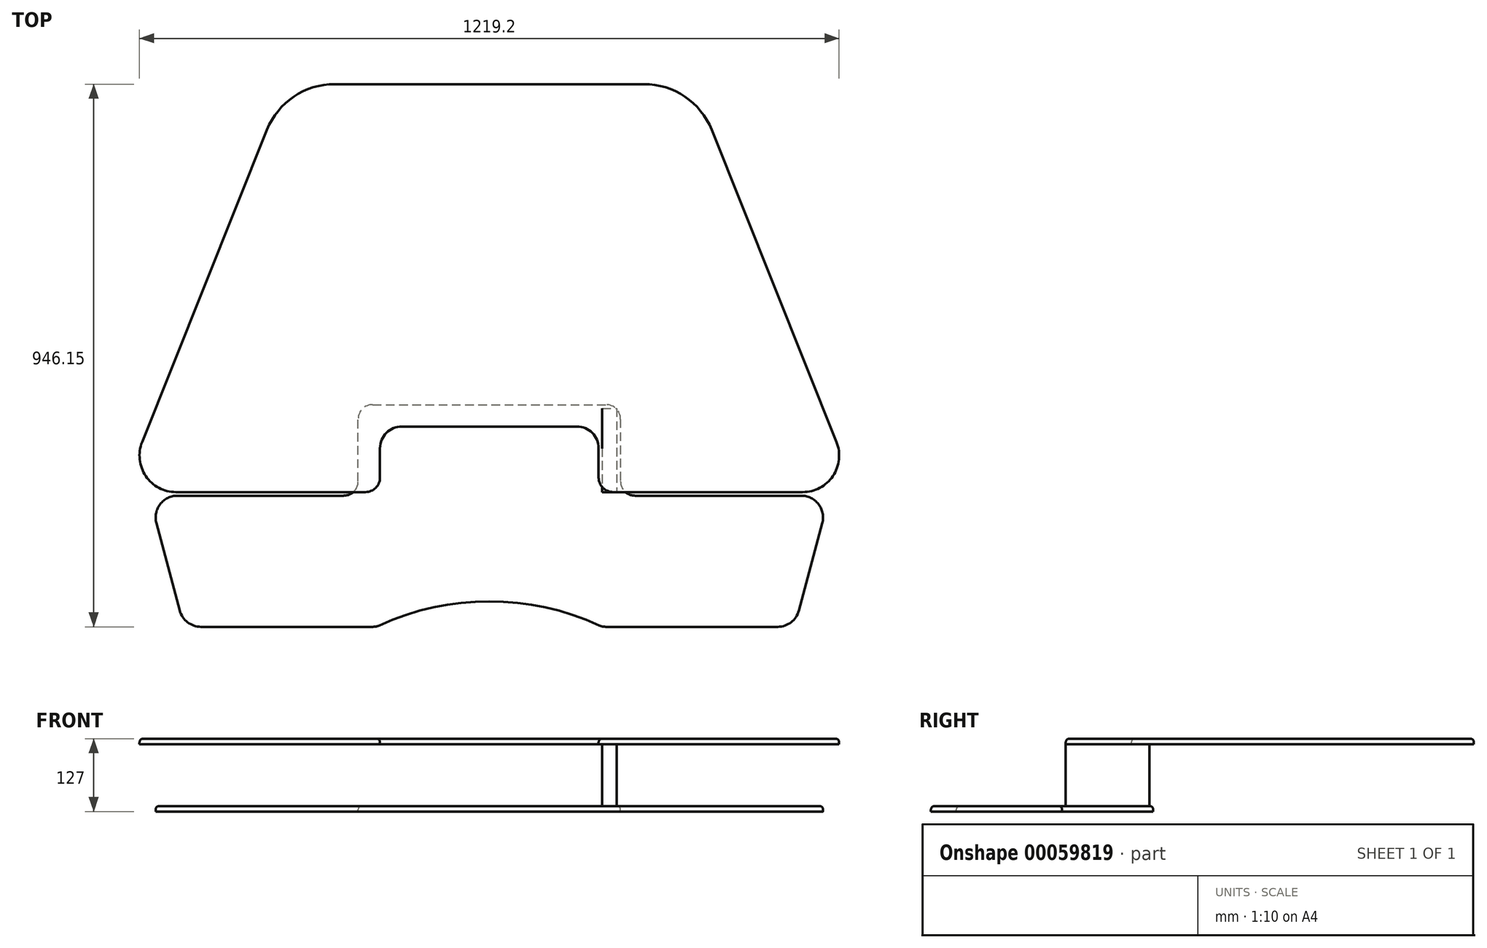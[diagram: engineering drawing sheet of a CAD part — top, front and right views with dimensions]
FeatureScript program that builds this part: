
annotation { "Feature Type Name" : "Feature", "Feature Type Description" : "" }
export const myFeature = defineFeature(function(context is Context, id is Id, definition is map)
    precondition{}
    {
        {
            var Q0;
            Q0=qCreatedBy(makeId("Top.planeOp"),FACE);
            var sketch = newSketch(context, id + "F0", { "sketchPlane" : qUnion([Q0])});
            skLineSegment(sketch, "E0", {"start": v(-190.5, 114.3) * mm, "end": v(190.5, 114.3) * mm});
            skLineSegment(sketch, "E1", {"start": v(190.5, 114.3) * mm, "end": v(190.5, 0) * mm});
            skLineSegment(sketch, "E2", {"start": v(190.5, 0) * mm, "end": v(546.1, 0) * mm});
            skLineSegment(sketch, "E3", {"start": v(605.06, 87.07) * mm, "end": v(355.6, 711.2) * mm});
            skLineSegment(sketch, "E4", {"start": v(355.6, 711.2) * mm, "end": v(-355.6, 711.2) * mm});
            skArc(sketch, "E5.filletArc", {"start": v(546.1, 0) * mm, "mid": v(598.68, 27.9) * mm, "end": v(605.06, 87.07) * mm});
            skLineSegment(sketch, "E6", {"start": v(0, 711.2) * mm, "end": v(0, 114.3) * mm, "construction": true});
            skLineSegment(sketch, "E7.MirrorCS", {"start": v(-605.06, 87.07) * mm, "end": v(-355.6, 711.2) * mm});
            skArc(sketch, "E8.MirrorCS", {"start": v(-546.1, 0) * mm, "mid": v(-598.68, 27.9) * mm, "end": v(-605.06, 87.07) * mm});
            skLineSegment(sketch, "E9.MirrorCS", {"start": v(-190.5, 0) * mm, "end": v(-546.1, 0) * mm});
            skLineSegment(sketch, "E10.MirrorCS", {"start": v(-190.5, 114.3) * mm, "end": v(-190.5, 0) * mm});
            skPoint(sketch, "E11.MirrorCS.end.orphan", {"position": v(0, 711.2) * mm});
            skPoint(sketch, "E11.MirrorCS.start.orphan", {"position": v(-355.6, 711.2) * mm});
            skPoint(sketch, "E12.MirrorCS.end.orphan", {"position": v(-190.5, 114.3) * mm});
            skPoint(sketch, "E12.MirrorCS.start.orphan", {"position": v(0, 114.3) * mm});
            skSolve(sketch);
        }
        {
            var Q0;
            Q0=qCreatedBy(makeId("Top.planeOp"),FACE);
            cPlane(context, id + "F1", {"entities" : qUnion([Q0]), "cplaneType" : CPlaneType.OFFSET, "offset" : 107.95 * mm, "oppositeDirection" : true, "width" : 152.4 * mm, "height" : 152.4 * mm});
        }
        {
            var Q0;
            Q0=qCreatedBy(id+"F1.planeOp",FACE);
            var sketch = newSketch(context, id + "F2", { "sketchPlane" : qUnion([Q0])});
            skLineSegment(sketch, "E13.bottom", {"start": v(-543.47, -6.35) * mm, "end": v(-254, -6.35) * mm});
            skLineSegment(sketch, "E13.top", {"start": v(-502.64, -234.95) * mm, "end": v(-202.3, -234.95) * mm});
            skLineSegment(sketch, "E13.left", {"start": v(-580.27, -54.31) * mm, "end": v(-539.44, -206.71) * mm});
            skLineSegment(sketch, "E13.right", {"start": v(580.27, -54.31) * mm, "end": v(539.44, -206.71) * mm});
            skLineSegment(sketch, "E14", {"start": v(-228.6, 19.05) * mm, "end": v(-228.6, 127) * mm});
            skLineSegment(sketch, "E15", {"start": v(-203.2, 152.4) * mm, "end": v(203.2, 152.4) * mm});
            skLineSegment(sketch, "E16", {"start": v(228.6, 127) * mm, "end": v(228.6, 19.05) * mm});
            skLineSegment(sketch, "E17.trimOffspring", {"start": v(254, -6.35) * mm, "end": v(543.47, -6.35) * mm});
            skPoint(sketch, "E18.visualSharp", {"position": v(-228.6, 152.4) * mm});
            skArc(sketch, "E18.filletArc", {"start": v(-203.2, 152.4) * mm, "mid": v(-221.16, 144.96) * mm, "end": v(-228.6, 127) * mm});
            skPoint(sketch, "E19.visualSharp", {"position": v(228.6, 152.4) * mm});
            skArc(sketch, "E19.filletArc", {"start": v(228.6, 127) * mm, "mid": v(221.16, 144.96) * mm, "end": v(203.2, 152.4) * mm});
            skPoint(sketch, "E20.visualSharp", {"position": v(228.6, -6.35) * mm});
            skArc(sketch, "E20.filletArc", {"start": v(228.6, 19.05) * mm, "mid": v(236.04, 1.09) * mm, "end": v(254, -6.35) * mm});
            skPoint(sketch, "E21.visualSharp", {"position": v(-228.6, -6.35) * mm});
            skArc(sketch, "E21.filletArc", {"start": v(-254, -6.35) * mm, "mid": v(-236.04, 1.09) * mm, "end": v(-228.6, 19.05) * mm});
            skArc(sketch, "E22", {"start": v(191.66, -232.61) * mm, "mid": v(0, -190.5) * mm, "end": v(-191.66, -232.61) * mm});
            skLineSegment(sketch, "E23.trimOffspring", {"start": v(202.3, -234.95) * mm, "end": v(502.64, -234.95) * mm});
            skPoint(sketch, "E24.visualSharp", {"position": v(-593.12, -6.35) * mm});
            skArc(sketch, "E24.filletArc", {"start": v(-543.47, -6.35) * mm, "mid": v(-573.7, -21.26) * mm, "end": v(-580.27, -54.31) * mm});
            skPoint(sketch, "E25.visualSharp", {"position": v(-531.87, -234.95) * mm});
            skArc(sketch, "E25.filletArc", {"start": v(-539.44, -206.71) * mm, "mid": v(-525.83, -227.08) * mm, "end": v(-502.64, -234.95) * mm});
            skPoint(sketch, "E26.visualSharp", {"position": v(531.87, -234.95) * mm});
            skArc(sketch, "E26.filletArc", {"start": v(502.64, -234.95) * mm, "mid": v(525.83, -227.08) * mm, "end": v(539.44, -206.71) * mm});
            skPoint(sketch, "E27.visualSharp", {"position": v(593.12, -6.35) * mm});
            skArc(sketch, "E27.filletArc", {"start": v(580.27, -54.31) * mm, "mid": v(573.7, -21.26) * mm, "end": v(543.47, -6.35) * mm});
            skPoint(sketch, "E28.visualSharp", {"position": v(-196.65, -234.95) * mm});
            skArc(sketch, "E28.filletArc", {"start": v(-202.3, -234.95) * mm, "mid": v(-196.85, -234.36) * mm, "end": v(-191.66, -232.61) * mm});
            skPoint(sketch, "E29.visualSharp", {"position": v(196.65, -234.95) * mm});
            skArc(sketch, "E29.filletArc", {"start": v(191.66, -232.61) * mm, "mid": v(196.85, -234.36) * mm, "end": v(202.3, -234.95) * mm});
            skSolve(sketch);
        }
        {
            var Q0;
            Q0=makeQuery(id+"F0.imprint","IMPRINT",FACE,{"disambiguationData":[TD([[makeQuery(id+"F0.imprint","IMPRINT",EDGE,{"derivedFrom":sQuery(id+"F0.wireOp",EDGE,"E0")}),1.0]])]});
            extrude(context, id + "F3", {"entities" : qUnion([Q0]), "depth" : 9.52 * mm});
        }
        {
            var Q0;
            Q0=makeQuery(id+"F3.opExtrude","SWEPT_EDGE",EDGE,{"disambiguationData":[OSD([sQuery(id+"F0.wireOp",EDGE,"E0"),sQuery(id+"F0.wireOp",EDGE,"E10.MirrorCS")])]});
            var Q1;
            Q1=makeQuery(id+"F3.opExtrude","SWEPT_EDGE",EDGE,{"disambiguationData":[OSD([sQuery(id+"F0.wireOp",EDGE,"E0"),sQuery(id+"F0.wireOp",EDGE,"E1")])]});
            fillet(context, id + "F4", {"entities" : qUnion([Q0, Q1]), "radius" : 38.1 * mm, "tangentPropagation" : true, "allowEdgeOverflow" : false});
        }
        {
            var Q0;
            Q0=makeQuery(id+"F3.opExtrude","SWEPT_EDGE",EDGE,{"disambiguationData":[OSD([sQuery(id+"F0.wireOp",EDGE,"E9.MirrorCS"),sQuery(id+"F0.wireOp",EDGE,"E10.MirrorCS")])]});
            var Q1;
            Q1=makeQuery(id+"F3.opExtrude","SWEPT_EDGE",EDGE,{"disambiguationData":[OSD([sQuery(id+"F0.wireOp",EDGE,"E1"),sQuery(id+"F0.wireOp",EDGE,"E2")])]});
            fillet(context, id + "F5", {"entities" : qUnion([Q0, Q1]), "radius" : 25.4 * mm, "tangentPropagation" : true, "allowEdgeOverflow" : false});
        }
        {
            var Q0;
            Q0=makeQuery(id+"F3.opExtrude","SWEPT_EDGE",EDGE,{"disambiguationData":[OSD([sQuery(id+"F0.wireOp",EDGE,"E3"),sQuery(id+"F0.wireOp",EDGE,"E4")])]});
            var Q1;
            Q1=makeQuery(id+"F3.opExtrude","SWEPT_EDGE",EDGE,{"disambiguationData":[OSD([sQuery(id+"F0.wireOp",EDGE,"E4"),sQuery(id+"F0.wireOp",EDGE,"E7.MirrorCS")])]});
            fillet(context, id + "F6", {"entities" : qUnion([Q0, Q1]), "radius" : 127 * mm, "tangentPropagation" : true, "allowEdgeOverflow" : false});
        }
        {
            var Q0;
            Q0=makeQuery(id+"F3.opExtrude","CAP_FACE",FACE,{"disambiguationData":[OSD([sQuery(id+"F0.wireOp",EDGE,"E0"),sQuery(id+"F0.wireOp",EDGE,"E1"),sQuery(id+"F0.wireOp",EDGE,"E2"),sQuery(id+"F0.wireOp",EDGE,"E3"),sQuery(id+"F0.wireOp",EDGE,"E4"),sQuery(id+"F0.wireOp",EDGE,"E5.filletArc"),sQuery(id+"F0.wireOp",EDGE,"E7.MirrorCS"),sQuery(id+"F0.wireOp",EDGE,"E8.MirrorCS"),sQuery(id+"F0.wireOp",EDGE,"E9.MirrorCS"),sQuery(id+"F0.wireOp",EDGE,"E10.MirrorCS")])],"isStart":false});
            fillet(context, id + "F7", {"entities" : qUnion([Q0]), "radius" : 6.35 * mm, "tangentPropagation" : true, "allowEdgeOverflow" : false});
        }
        {
            var Q0;
            Q0 = qSketchRegion(id + "F2", true);
            extrude(context, id + "F8", {"entities" : qUnion([Q0]), "oppositeDirection" : true, "depth" : 9.52 * mm});
        }
        {
            var Q0;
            Q0=makeQuery(id+"F8.opExtrude","CAP_FACE",FACE,{"disambiguationData":[OSD([sQuery(id+"F2.wireOp",EDGE,"E13.bottom"),sQuery(id+"F2.wireOp",EDGE,"E13.top"),sQuery(id+"F2.wireOp",EDGE,"E13.left"),sQuery(id+"F2.wireOp",EDGE,"E13.right"),sQuery(id+"F2.wireOp",EDGE,"E14"),sQuery(id+"F2.wireOp",EDGE,"E15"),sQuery(id+"F2.wireOp",EDGE,"E16"),sQuery(id+"F2.wireOp",EDGE,"E17.trimOffspring"),sQuery(id+"F2.wireOp",EDGE,"E18.filletArc"),sQuery(id+"F2.wireOp",EDGE,"E19.filletArc"),sQuery(id+"F2.wireOp",EDGE,"E20.filletArc"),sQuery(id+"F2.wireOp",EDGE,"E21.filletArc"),sQuery(id+"F2.wireOp",EDGE,"E22"),sQuery(id+"F2.wireOp",EDGE,"E23.trimOffspring"),sQuery(id+"F2.wireOp",EDGE,"E24.filletArc"),sQuery(id+"F2.wireOp",EDGE,"E25.filletArc"),sQuery(id+"F2.wireOp",EDGE,"E26.filletArc"),sQuery(id+"F2.wireOp",EDGE,"E27.filletArc"),sQuery(id+"F2.wireOp",EDGE,"E28.filletArc"),sQuery(id+"F2.wireOp",EDGE,"E29.filletArc")])],"isStart":true});
            fillet(context, id + "F9", {"entities" : qUnion([Q0]), "radius" : 6.35 * mm, "tangentPropagation" : true, "allowEdgeOverflow" : false});
        }
        {
            var Q0;
            Q0=makeQuery(id+"F8.opExtrude","CAP_FACE",FACE,{"disambiguationData":[OSD([sQuery(id+"F2.wireOp",EDGE,"E13.bottom"),sQuery(id+"F2.wireOp",EDGE,"E13.top"),sQuery(id+"F2.wireOp",EDGE,"E13.left"),sQuery(id+"F2.wireOp",EDGE,"E13.right"),sQuery(id+"F2.wireOp",EDGE,"E14"),sQuery(id+"F2.wireOp",EDGE,"E15"),sQuery(id+"F2.wireOp",EDGE,"E16"),sQuery(id+"F2.wireOp",EDGE,"E17.trimOffspring"),sQuery(id+"F2.wireOp",EDGE,"E18.filletArc"),sQuery(id+"F2.wireOp",EDGE,"E19.filletArc"),sQuery(id+"F2.wireOp",EDGE,"E20.filletArc"),sQuery(id+"F2.wireOp",EDGE,"E21.filletArc"),sQuery(id+"F2.wireOp",EDGE,"E22"),sQuery(id+"F2.wireOp",EDGE,"E23.trimOffspring"),sQuery(id+"F2.wireOp",EDGE,"E24.filletArc"),sQuery(id+"F2.wireOp",EDGE,"E25.filletArc"),sQuery(id+"F2.wireOp",EDGE,"E26.filletArc"),sQuery(id+"F2.wireOp",EDGE,"E27.filletArc"),sQuery(id+"F2.wireOp",EDGE,"E28.filletArc"),sQuery(id+"F2.wireOp",EDGE,"E29.filletArc")])],"isStart":true});
            var sketch = newSketch(context, id + "F10", { "sketchPlane" : qUnion([Q0])});
            skLineSegment(sketch, "E30.bottom", {"start": v(196.85, 146.05) * mm, "end": v(222.25, 146.05) * mm});
            skLineSegment(sketch, "E30.top", {"start": v(196.85, 0) * mm, "end": v(222.25, 0) * mm});
            skLineSegment(sketch, "E30.left", {"start": v(196.85, 146.05) * mm, "end": v(196.85, 0) * mm});
            skLineSegment(sketch, "E30.right", {"start": v(222.25, 146.05) * mm, "end": v(222.25, 0) * mm});
            skSolve(sketch);
        }
        {
            var Q0;
            Q0 = qSketchRegion(id + "F10", true);
            var Q1;
            Q1=makeQuery(id+"F3.opExtrude","CAP_FACE",FACE,{"disambiguationData":[OSD([sQuery(id+"F0.wireOp",EDGE,"E0"),sQuery(id+"F0.wireOp",EDGE,"E1"),sQuery(id+"F0.wireOp",EDGE,"E2"),sQuery(id+"F0.wireOp",EDGE,"E3"),sQuery(id+"F0.wireOp",EDGE,"E4"),sQuery(id+"F0.wireOp",EDGE,"E5.filletArc"),sQuery(id+"F0.wireOp",EDGE,"E7.MirrorCS"),sQuery(id+"F0.wireOp",EDGE,"E8.MirrorCS"),sQuery(id+"F0.wireOp",EDGE,"E9.MirrorCS"),sQuery(id+"F0.wireOp",EDGE,"E10.MirrorCS")])],"isStart":true});
            extrude(context, id + "F11", {"entities" : qUnion([Q0]), "endBound" : BoundingType.UP_TO_SURFACE, "endBoundEntityFace" : qUnion([Q1]), "depth" : 25.4 * mm});
        }
    });
